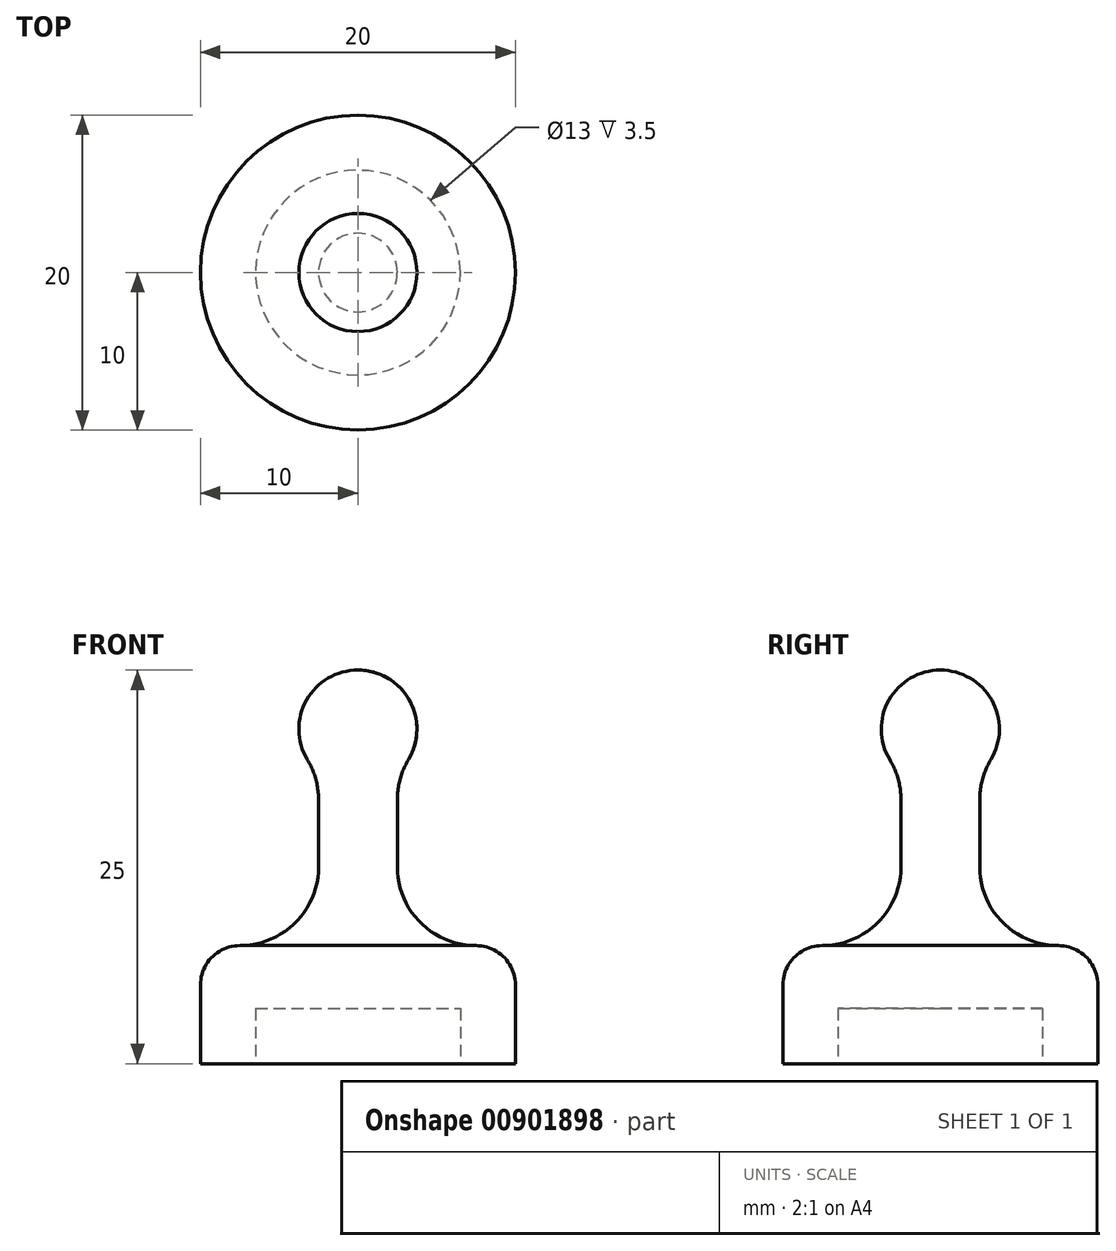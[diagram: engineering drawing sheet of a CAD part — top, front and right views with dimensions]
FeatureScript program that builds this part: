
annotation { "Feature Type Name" : "Feature", "Feature Type Description" : "" }
export const myFeature = defineFeature(function(context is Context, id is Id, definition is map)
    precondition{}
    {
        {
            var Q0;
            Q0=qCreatedBy(makeId("Front.planeOp"),FACE);
            var sketch = newSketch(context, id + "F0", { "sketchPlane" : qUnion([Q0])});
            skLineSegment(sketch, "E0", {"start": v(0, 0) * mm, "end": v(0, 25) * mm});
            skLineSegment(sketch, "E1", {"start": v(0, 0) * mm, "end": v(-10, 0) * mm});
            skLineSegment(sketch, "E2", {"start": v(-10, 0) * mm, "end": v(-10, 5) * mm});
            skArc(sketch, "E3", {"start": v(0, 25) * mm, "mid": v(-3.26, 23.1) * mm, "end": v(-3.21, 19.32) * mm});
            skLineSegment(sketch, "E4", {"start": v(-2.5, 16.74) * mm, "end": v(-2.5, 12.5) * mm});
            skLineSegment(sketch, "E5", {"start": v(-7.5, 7.5) * mm, "end": v(-7.5, 7.5) * mm});
            skPoint(sketch, "E6.visualSharp", {"position": v(-2.5, 18.45) * mm});
            skArc(sketch, "E6.filletArc", {"start": v(-2.5, 16.74) * mm, "mid": v(-2.68, 18.08) * mm, "end": v(-3.21, 19.32) * mm});
            skPoint(sketch, "E7.visualSharp", {"position": v(-2.5, 7.5) * mm});
            skArc(sketch, "E7.filletArc", {"start": v(-7.5, 7.5) * mm, "mid": v(-3.96, 8.96) * mm, "end": v(-2.5, 12.5) * mm});
            skPoint(sketch, "E8.visualSharp", {"position": v(-10, 7.5) * mm});
            skArc(sketch, "E8.filletArc", {"start": v(-7.5, 7.5) * mm, "mid": v(-9.27, 6.77) * mm, "end": v(-10, 5) * mm});
            skSolve(sketch);
        }
        {
            var Q0;
            Q0=makeQuery(id+"F0.imprint","IMPRINT",FACE,{"disambiguationData":[TD([[makeQuery(id+"F0.imprint","IMPRINT",EDGE,{"derivedFrom":sQuery(id+"F0.wireOp",EDGE,"E0")}),1.0]])]});
            var Q1;
            Q1=sQuery(id+"F0.wireOp",EDGE,"E0");
            revolve(context, id + "F1", {"surfaceOperationType" : NewSurfaceOperationType.NEW, "entities" : qUnion([Q0]), "axis" : qUnion([Q1]), "revolveType" : RevolveType.FULL});
        }
        {
            var Q0;
            Q0=makeQuery(id+"F1.opRevolve","SWEPT_FACE",FACE,{"disambiguationData":[OSD([sQuery(id+"F0.wireOp",EDGE,"E1")])]});
            var sketch = newSketch(context, id + "F2", { "sketchPlane" : qUnion([Q0])});
            skCircle(sketch, "E9", {"center": v(0, 0) * mm, "radius": 6.5 * mm});
            skSolve(sketch);
        }
        {
            var Q0;
            Q0=makeQuery(id+"F2.imprint","IMPRINT",FACE,{"disambiguationData":[TD([[makeQuery(id+"F2.imprint","IMPRINT",EDGE,{"derivedFrom":sQuery(id+"F2.wireOp",EDGE,"E9")}),1.0]])]});
            extrude(context, id + "F3", {"entities" : qUnion([Q0]), "operationType" : NewBodyOperationType.REMOVE, "oppositeDirection" : true, "depth" : 3.5 * mm, "offsetDistance" : 25 * mm});
        }
    });
